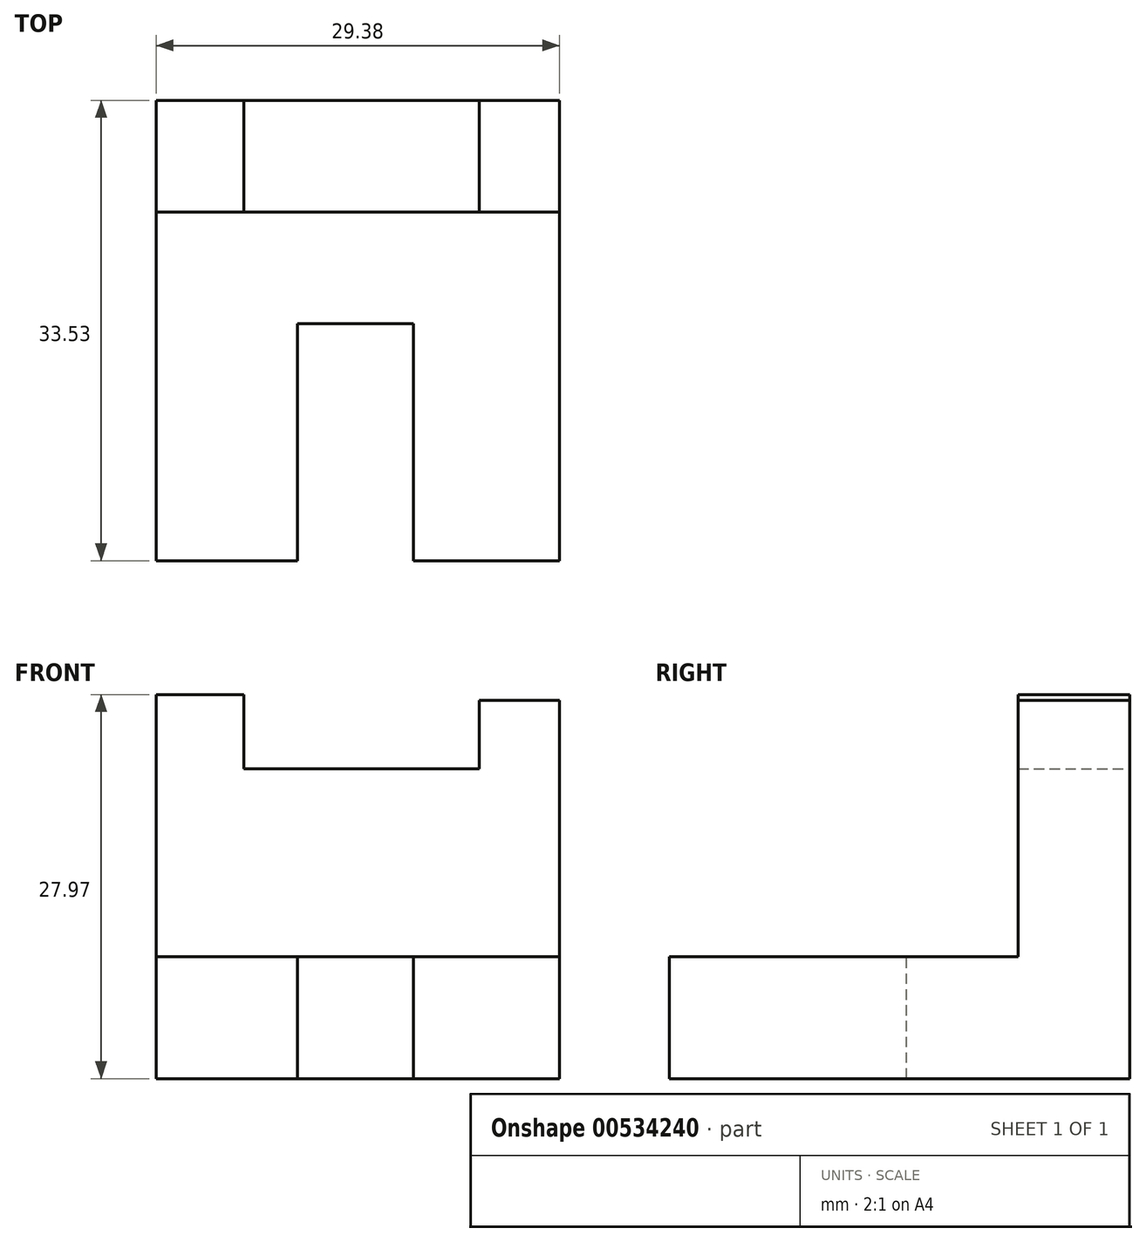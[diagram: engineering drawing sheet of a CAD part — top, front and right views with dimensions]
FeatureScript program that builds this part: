
annotation { "Feature Type Name" : "Feature", "Feature Type Description" : "" }
export const myFeature = defineFeature(function(context is Context, id is Id, definition is map)
    precondition{}
    {
        {
            var Q0;
            Q0=qCreatedBy(makeId("Front.planeOp"),FACE);
            var sketch = newSketch(context, id + "F0", { "sketchPlane" : qUnion([Q0])});
            skLineSegment(sketch, "E0", {"start": v(0, 0) * mm, "end": v(0, 5.42) * mm});
            skLineSegment(sketch, "E1", {"start": v(0, 5.42) * mm, "end": v(6.4, 5.42) * mm});
            skLineSegment(sketch, "E2", {"start": v(6.4, 5.42) * mm, "end": v(6.4, 0) * mm});
            skLineSegment(sketch, "E3", {"start": v(6.4, 0) * mm, "end": v(23.53, 0) * mm});
            skLineSegment(sketch, "E4", {"start": v(23.53, 0) * mm, "end": v(23.53, 4.99) * mm});
            skLineSegment(sketch, "E5", {"start": v(23.53, 4.99) * mm, "end": v(29.38, 4.99) * mm});
            skLineSegment(sketch, "E6", {"start": v(29.38, 4.99) * mm, "end": v(29.38, -22.55) * mm});
            skLineSegment(sketch, "E7", {"start": v(29.38, -22.55) * mm, "end": v(0, -22.55) * mm});
            skLineSegment(sketch, "E8", {"start": v(0, -22.55) * mm, "end": v(0, 0) * mm});
            skSolve(sketch);
        }
        {
            var Q0;
            Q0=makeQuery(id+"F0.imprint","IMPRINT",FACE,{"disambiguationData":[TD([[makeQuery(id+"F0.imprint","IMPRINT",EDGE,{"derivedFrom":sQuery(id+"F0.wireOp",EDGE,"E0")}),-1.0]])]});
            extrude(context, id + "F1", {"entities" : qUnion([Q0]), "depth" : 8.13 * mm, "offsetDistance" : 25.4 * mm});
        }
        {
            var Q0;
            Q0=makeQuery(id+"F1.opExtrude","CAP_FACE",FACE,{"disambiguationData":[OSD([sQuery(id+"F0.wireOp",EDGE,"E0"),sQuery(id+"F0.wireOp",EDGE,"E1"),sQuery(id+"F0.wireOp",EDGE,"E2"),sQuery(id+"F0.wireOp",EDGE,"E3"),sQuery(id+"F0.wireOp",EDGE,"E4"),sQuery(id+"F0.wireOp",EDGE,"E5"),sQuery(id+"F0.wireOp",EDGE,"E6"),sQuery(id+"F0.wireOp",EDGE,"E7"),sQuery(id+"F0.wireOp",EDGE,"E8")])],"isStart":false});
            var sketch = newSketch(context, id + "F2", { "sketchPlane" : qUnion([Q0])});
            skLineSegment(sketch, "E9", {"start": v(0, -13.66) * mm, "end": v(29.38, -13.66) * mm});
            skLineSegment(sketch, "E10", {"start": v(29.38, -13.66) * mm, "end": v(29.38, -22.55) * mm});
            skLineSegment(sketch, "E11", {"start": v(29.38, -22.55) * mm, "end": v(0, -22.55) * mm});
            skLineSegment(sketch, "E12", {"start": v(0, -22.55) * mm, "end": v(0, -13.66) * mm});
            skSolve(sketch);
        }
        {
            var Q0;
            Q0 = qSketchRegion(id + "F2", true);
            extrude(context, id + "F3", {"entities" : qUnion([Q0]), "operationType" : NewBodyOperationType.ADD, "depth" : 25.4 * mm, "offsetDistance" : 25.4 * mm});
        }
        {
            var Q0;
            Q0=makeQuery(id+"F3.opExtrude","SWEPT_FACE",FACE,{"disambiguationData":[OSD([sQuery(id+"F2.wireOp",EDGE,"E9")])]});
            var sketch = newSketch(context, id + "F4", { "sketchPlane" : qUnion([Q0])});
            skLineSegment(sketch, "E13", {"start": v(18.76, -33.53) * mm, "end": v(18.76, -16.05) * mm});
            skLineSegment(sketch, "E14", {"start": v(18.76, -16.05) * mm, "end": v(11.82, -16.05) * mm});
            skLineSegment(sketch, "E15", {"start": v(11.82, -16.05) * mm, "end": v(11.82, -33.53) * mm});
            skSolve(sketch);
        }
        {
            var Q0;
            Q0 = qSketchRegion(id + "F4", true);
            var Q1;
            {var subQ0=sQuery(id+"F4.wireOp",EDGE,"E13");Q1=makeQuery(id+"F4.imprint","IMPRINT",FACE,{"disambiguationData":[TD([[makeQuery(id+"F4.imprint","IMPRINT",EDGE,{"derivedFrom":subQ0}),1.0]])]});}
            extrude(context, id + "F5", {"entities" : qUnion([Q0, Q1]), "operationType" : NewBodyOperationType.ADD, "oppositeDirection" : true, "depth" : 8.38 * mm, "offsetDistance" : 25.4 * mm});
        }
        {
            var Q0;
            Q0=makeQuery(id+"F3.opExtrude","SWEPT_FACE",FACE,{"disambiguationData":[OSD([sQuery(id+"F2.wireOp",EDGE,"E9")])]});
            var sketch = newSketch(context, id + "F6", { "sketchPlane" : qUnion([Q0])});
            skLineSegment(sketch, "E16", {"start": v(10.3, -33.53) * mm, "end": v(10.3, -16.26) * mm});
            skLineSegment(sketch, "E17", {"start": v(10.3, -16.26) * mm, "end": v(18.76, -16.26) * mm});
            skLineSegment(sketch, "E18", {"start": v(18.76, -16.26) * mm, "end": v(18.76, -33.53) * mm});
            skSolve(sketch);
        }
        {
            var Q0;
            {var subQ0=sQuery(id+"F6.wireOp",EDGE,"E16");Q0=makeQuery(id+"F6.imprint","IMPRINT",FACE,{"disambiguationData":[TD([[makeQuery(id+"F6.imprint","IMPRINT",EDGE,{"derivedFrom":subQ0}),-1.0]])]});}
            extrude(context, id + "F7", {"entities" : qUnion([Q0]), "operationType" : NewBodyOperationType.REMOVE, "oppositeDirection" : true, "depth" : 9.9 * mm, "offsetDistance" : 25.4 * mm});
        }
    });
